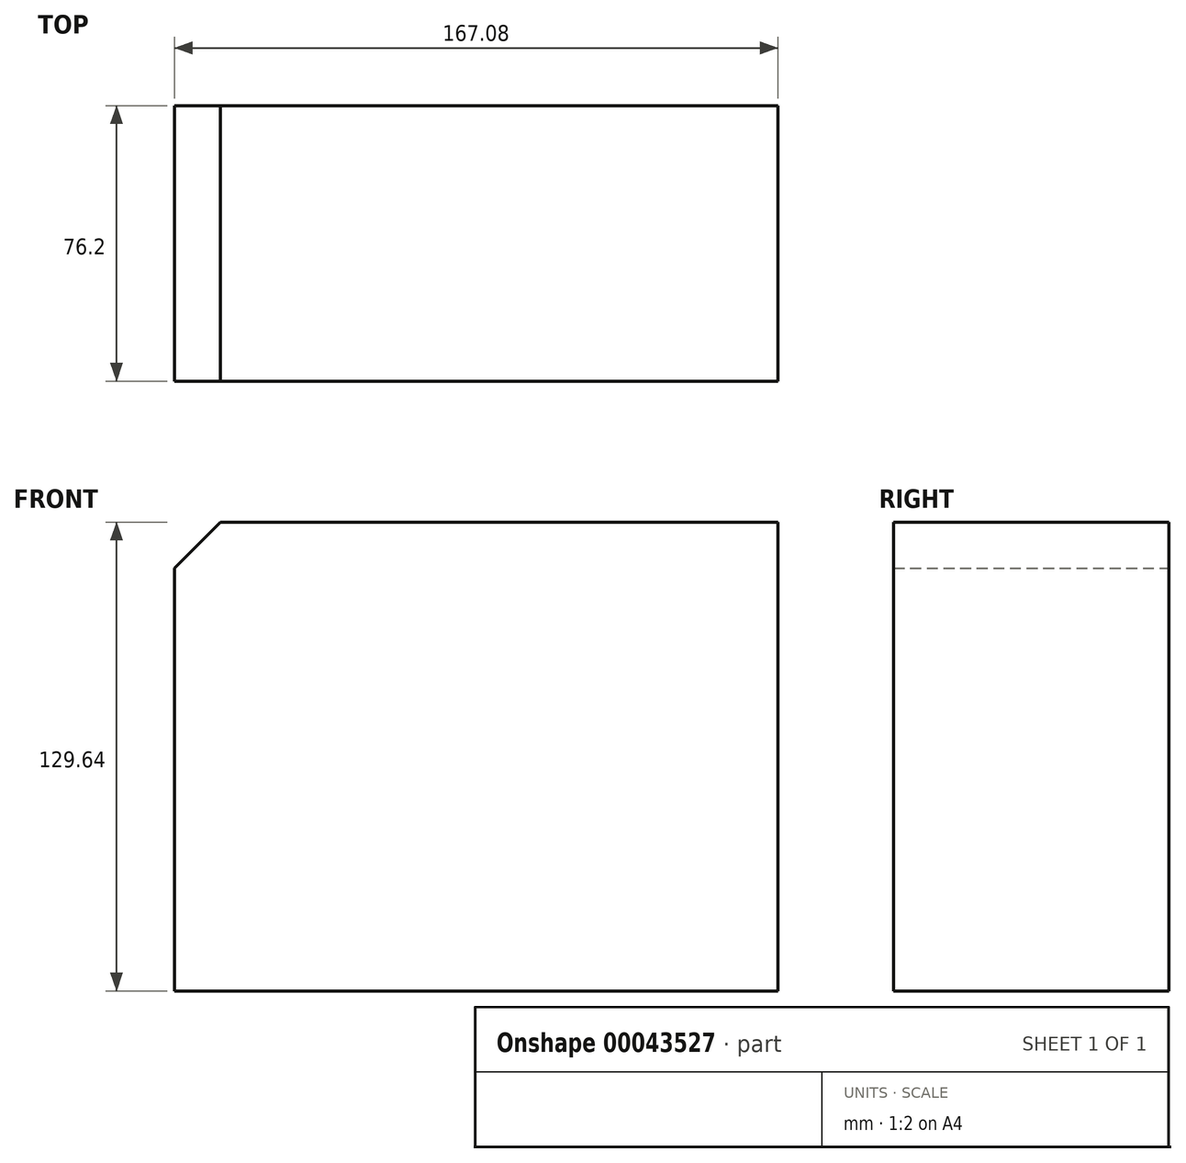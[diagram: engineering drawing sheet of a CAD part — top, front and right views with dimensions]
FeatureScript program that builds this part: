
annotation { "Feature Type Name" : "Feature", "Feature Type Description" : "" }
export const myFeature = defineFeature(function(context is Context, id is Id, definition is map)
    precondition{}
    {
        {
            var Q0;
            Q0=qCreatedBy(makeId("Front.planeOp"),FACE);
            var sketch = newSketch(context, id + "F0", { "sketchPlane" : qUnion([Q0])});
            skLineSegment(sketch, "E0.bottom", {"start": v(-43.13, 84.46) * mm, "end": v(123.95, 84.46) * mm});
            skLineSegment(sketch, "E0.top", {"start": v(-43.13, -45.18) * mm, "end": v(123.95, -45.18) * mm});
            skLineSegment(sketch, "E0.left", {"start": v(-43.13, 84.46) * mm, "end": v(-43.13, -45.18) * mm});
            skLineSegment(sketch, "E0.right", {"start": v(123.95, 84.46) * mm, "end": v(123.95, -45.18) * mm});
            skSolve(sketch);
        }
        {
            var Q0;
            Q0=qSketchRegion(id+"F0",true);
            extrude(context, id + "F1", {"entities" : qUnion([Q0]), "depth" : 76.2 * mm});
        }
        {
            var Q0;
            Q0=makeQuery(id+"F1.opExtrude","SWEPT_EDGE",EDGE,{"disambiguationData":[OSD([sQuery(id+"F0.wireOp",EDGE,"E0.bottom"),sQuery(id+"F0.wireOp",EDGE,"E0.left")])]});
            chamfer(context, id + "F2", {"entities" : qUnion([Q0]), "width" : 12.7 * mm, "tangentPropagation" : true});
        }
    });
